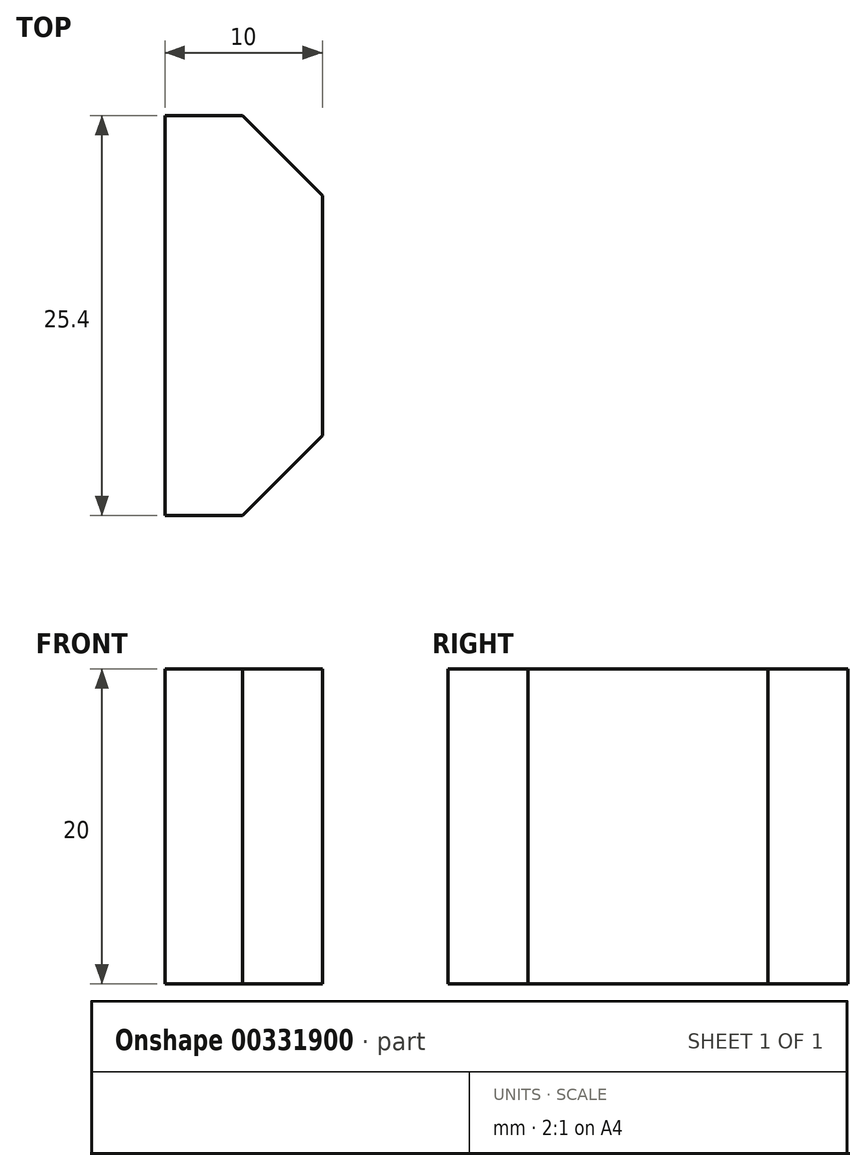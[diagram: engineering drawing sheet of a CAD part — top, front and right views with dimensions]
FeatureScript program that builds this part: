
annotation { "Feature Type Name" : "Feature", "Feature Type Description" : "" }
export const myFeature = defineFeature(function(context is Context, id is Id, definition is map)
    precondition{}
    {
        {
            var Q0;
            Q0=qCreatedBy(makeId("Front.planeOp"),FACE);
            var sketch = newSketch(context, id + "F0", { "sketchPlane" : qUnion([Q0])});
            skLineSegment(sketch, "E0.bottom", {"start": v(0, 0) * mm, "end": v(10, 0) * mm});
            skLineSegment(sketch, "E0.top", {"start": v(0, 20) * mm, "end": v(10, 20) * mm});
            skLineSegment(sketch, "E0.left", {"start": v(0, 0) * mm, "end": v(0, 20) * mm});
            skLineSegment(sketch, "E0.right", {"start": v(10, 0) * mm, "end": v(10, 20) * mm});
            skSolve(sketch);
        }
        {
            var Q0;
            Q0=makeQuery(id+"F0.imprint","IMPRINT",FACE,{"disambiguationData":[TD([[makeQuery(id+"F0.imprint","IMPRINT",EDGE,{"derivedFrom":sQuery(id+"F0.wireOp",EDGE,"E0.bottom")}),1.0]])]});
            extrude(context, id + "F1", {"entities" : qUnion([Q0]), "depth" : 25.4 * mm});
        }
        {
            var Q0;
            Q0=makeQuery(id+"F1.opExtrude","CAP_EDGE",EDGE,{"disambiguationData":[OSD([sQuery(id+"F0.wireOp",EDGE,"E0.right")])],"isStart":false});
            var Q1;
            Q1=makeQuery(id+"F1.opExtrude","CAP_EDGE",EDGE,{"disambiguationData":[OSD([sQuery(id+"F0.wireOp",EDGE,"E0.right")])],"isStart":true});
            chamfer(context, id + "F2", {"entities" : qUnion([Q0, Q1]), "width" : 5.08 * mm, "tangentPropagation" : true});
        }
    });
